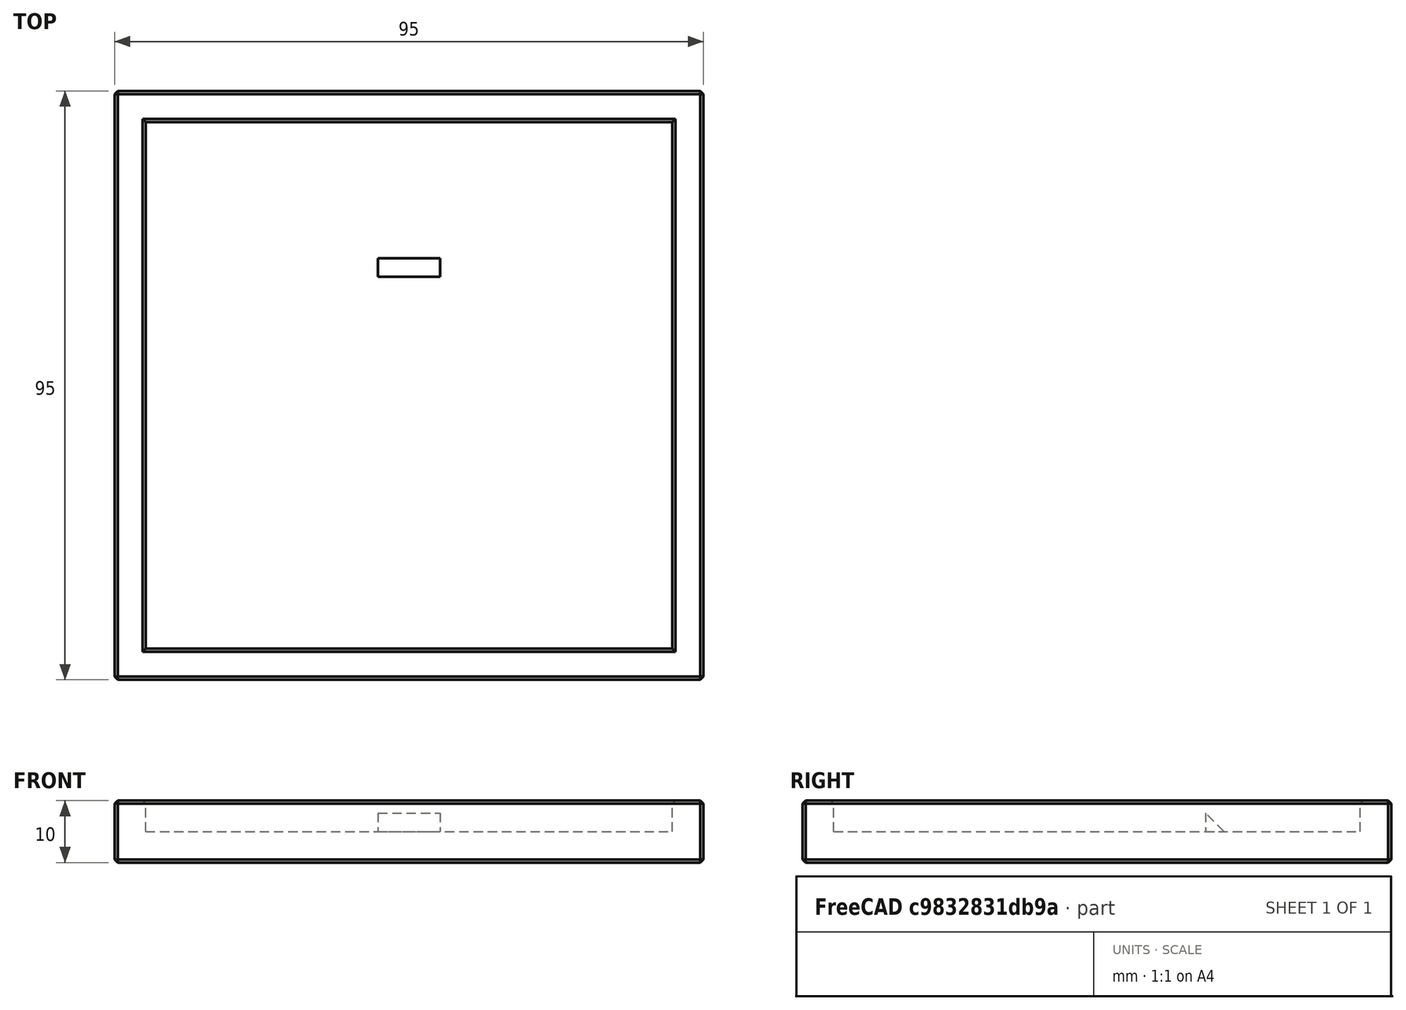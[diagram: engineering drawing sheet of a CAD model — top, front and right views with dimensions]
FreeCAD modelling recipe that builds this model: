
FCSTD DOCUMENT  (FreeCAD 0.18R14555 (Git shallow))
Label: planter-tray
License: All rights reserved
LicenseURL: http://en.wikipedia.org/wiki/All_rights_reserved
objects: Part::Box×2, Part::Cut×1, Part::Feature×1, Part::Chamfer×1, Part::MultiFuse×1
note: 6 computed .brp shape members not serialized (recipe doc carries the construction recipe); baked Part::Feature solids carry a one-line shape summary decoded from their .brp

FEATURE [Part::Box] Box  label="Cube"
  AttacherType = Attacher::AttachEngine3D
  Height = 10
  Length = 95
  Width = 95
FEATURE [Part::Box] Box001  label="Cube001"
  AttacherType = Attacher::AttachEngine3D
  Height = 5
  Length = 85
  Placement = pos=(5,5,5) rot=(0,0,1;0rad)
  Width = 85
FEATURE [Part::Cut] Cut
  Base = -> Box
  Tool = -> Box001
FEATURE [Part::Feature] Body001
  Placement = pos=(42.5,-38,1) rot=(0,0,1;0rad)
  shape: bbox 10 x 3 x 3 mm, 5 faces (baked)
FEATURE [Part::Chamfer] Chamfer
  Base = -> Cut
  Edges = 16 edges r=0.5: [Edge1,Edge2,Edge3,Edge4,Edge5,Edge6,Edge7,Edge8,Edge9,Edge10,Edge11,Edge12,Edge13,Edge14,Edge15,Edge16]
FEATURE [Part::MultiFuse] Fusion
  Shapes = -> [Body001,Chamfer]
